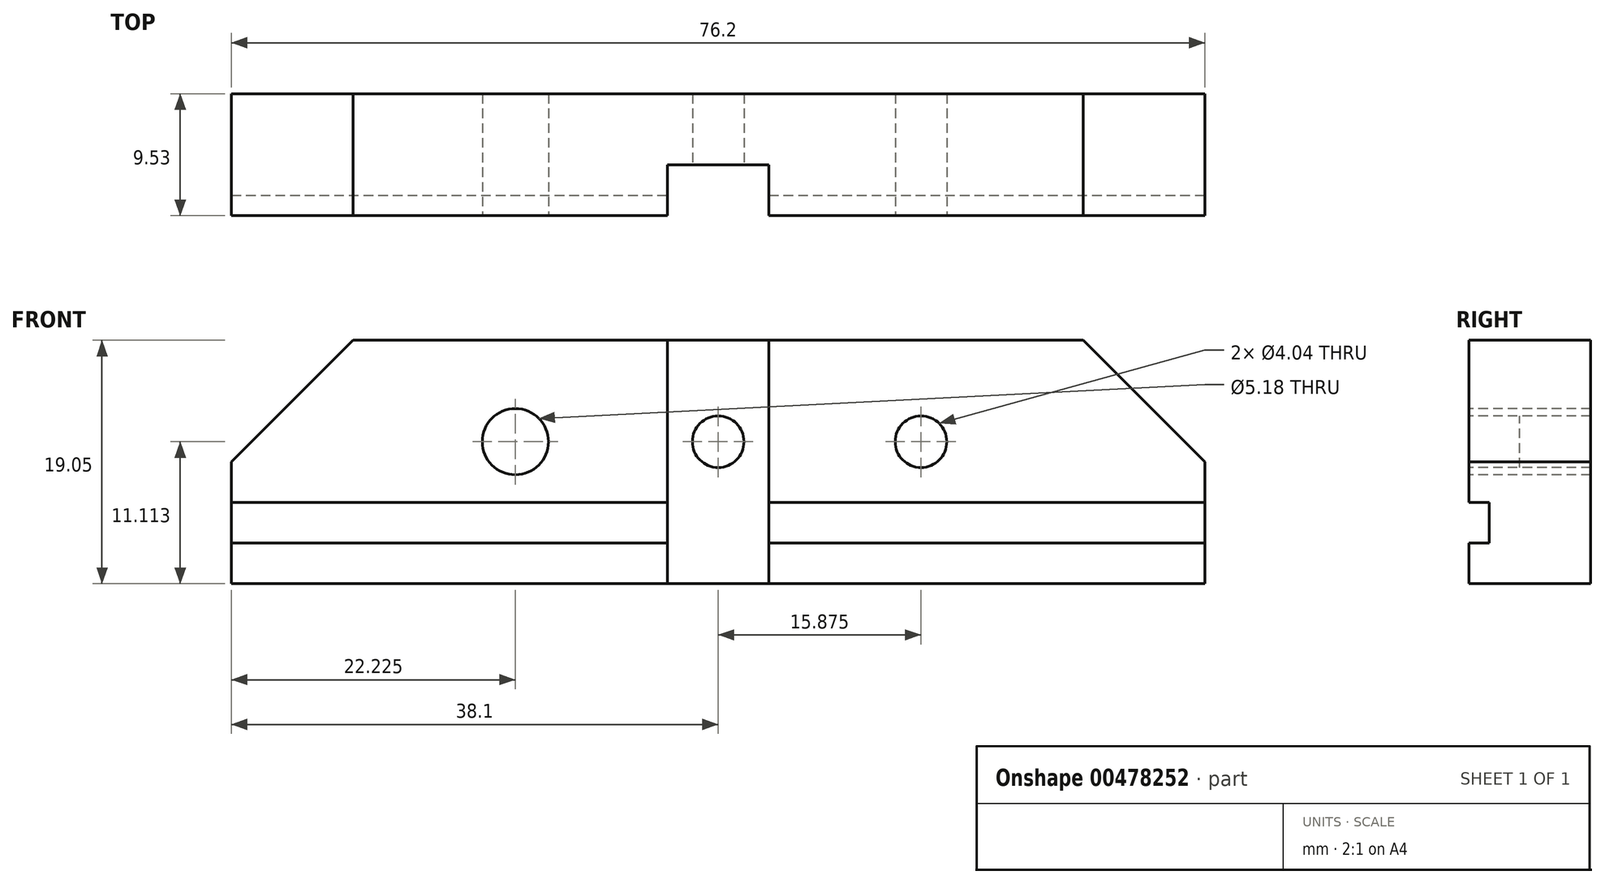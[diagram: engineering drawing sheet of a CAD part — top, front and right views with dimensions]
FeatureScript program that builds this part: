
annotation { "Feature Type Name" : "Feature", "Feature Type Description" : "" }
export const myFeature = defineFeature(function(context is Context, id is Id, definition is map)
    precondition{}
    {
        {
            var Q0;
            Q0=qCreatedBy(makeId("Front.planeOp"),FACE);
            var sketch = newSketch(context, id + "F0", { "sketchPlane" : qUnion([Q0])});
            skLineSegment(sketch, "E0.bottom", {"start": v(-38.1, 19.05) * mm, "end": v(38.1, 19.05) * mm});
            skLineSegment(sketch, "E0.top", {"start": v(-38.1, 0) * mm, "end": v(38.1, 0) * mm});
            skLineSegment(sketch, "E0.left", {"start": v(-38.1, 19.05) * mm, "end": v(-38.1, 0) * mm});
            skLineSegment(sketch, "E0.right", {"start": v(38.1, 19.05) * mm, "end": v(38.1, 0) * mm});
            skLineSegment(sketch, "E1", {"start": v(38.1, 11.11) * mm, "end": v(-38.1, 11.11) * mm, "construction": true});
            skLineSegment(sketch, "E2", {"start": v(-38.1, 6.35) * mm, "end": v(38.1, 6.35) * mm});
            skLineSegment(sketch, "E3", {"start": v(-38.1, 3.17) * mm, "end": v(38.1, 3.18) * mm});
            skLineSegment(sketch, "E4", {"start": v(-38.1, 4.76) * mm, "end": v(38.1, 4.76) * mm, "construction": true});
            skLineSegment(sketch, "E5", {"start": v(-3.97, 19.05) * mm, "end": v(-3.97, 0) * mm});
            skLineSegment(sketch, "E6", {"start": v(3.97, 0) * mm, "end": v(3.97, 19.05) * mm});
            skLineSegment(sketch, "E7", {"start": v(0, 19.05) * mm, "end": v(0, 0) * mm, "construction": true});
            skCircle(sketch, "E8", {"center": v(-15.88, 11.11) * mm, "radius": 2.6 * mm});
            skCircle(sketch, "E9", {"center": v(15.88, 11.11) * mm, "radius": 2.02 * mm});
            skCircle(sketch, "E10", {"center": v(0, 11.11) * mm, "radius": 2.02 * mm});
            skSolve(sketch);
        }
        {
            var Q0;
            Q0 = qSketchRegion(id + "F0", true);
            var Q1;
            {var subQ0=sQuery(id+"F0.wireOp",EDGE,"E5");var subQ1=sQuery(id+"F0.wireOp",EDGE,"E2");var subQ2=makeQuery(id+"F0.imprint","INTERSECT",VERTEX,{"derivedFrom":[subQ1,subQ0]});Q1=makeQuery(id+"F0.imprint","IMPRINT",FACE,{"disambiguationData":[TD([[makeQuery(id+"F0.imprint","IMPRINT",EDGE,{"disambiguationData":[TD([[subQ2,-1.0]])],"derivedFrom":subQ1}),-1.0]])]});}
            var Q2;
            Q2=makeQuery(id+"F0.imprint","IMPRINT",FACE,{"disambiguationData":[TD([[makeQuery(id+"F0.imprint","IMPRINT",EDGE,{"derivedFrom":sQuery(id+"F0.wireOp",EDGE,"E10")}),1.0]])]});
            var Q3;
            Q3=makeQuery(id+"F0.imprint","IMPRINT",FACE,{"disambiguationData":[TD([[makeQuery(id+"F0.imprint","IMPRINT",EDGE,{"derivedFrom":sQuery(id+"F0.wireOp",EDGE,"E9")}),1.0]])]});
            extrude(context, id + "F1", {"entities" : qUnion([Q0, Q1, Q2, Q3]), "oppositeDirection" : true, "depth" : 9.52 * mm, "offsetDistance" : 25.4 * mm});
        }
        {
            var Q0;
            Q0=makeQuery(id+"F0.imprint","IMPRINT",FACE,{"disambiguationData":[TD([[makeQuery(id+"F0.imprint","IMPRINT",EDGE,{"derivedFrom":sQuery(id+"F0.wireOp",EDGE,"E10")}),-1.0]])]});
            var Q1;
            {var subQ0=sQuery(id+"F0.wireOp",EDGE,"E5");var subQ1=sQuery(id+"F0.wireOp",EDGE,"E2");var subQ2=makeQuery(id+"F0.imprint","INTERSECT",VERTEX,{"derivedFrom":[subQ1,subQ0]});Q1=makeQuery(id+"F0.imprint","IMPRINT",FACE,{"disambiguationData":[TD([[makeQuery(id+"F0.imprint","IMPRINT",EDGE,{"disambiguationData":[TD([[subQ2,-1.0]])],"derivedFrom":subQ1}),-1.0]])]});}
            var Q2;
            {var subQ0=sQuery(id+"F0.wireOp",EDGE,"E5");var subQ1=sQuery(id+"F0.wireOp",EDGE,"E0.top");var subQ2=makeQuery(id+"F0.imprint","INTERSECT",VERTEX,{"derivedFrom":[subQ1,subQ0]});Q2=makeQuery(id+"F0.imprint","IMPRINT",FACE,{"disambiguationData":[TD([[makeQuery(id+"F0.imprint","IMPRINT",EDGE,{"disambiguationData":[TD([[subQ2,-1.0]])],"derivedFrom":subQ1}),1.0]])]});}
            extrude(context, id + "F2", {"entities" : qUnion([Q0, Q1, Q2]), "operationType" : NewBodyOperationType.REMOVE, "oppositeDirection" : true, "depth" : 3.96 * mm, "offsetDistance" : 25.4 * mm});
        }
        {
            var Q0;
            {var subQ0=sQuery(id+"F0.wireOp",EDGE,"E2");var subQ1=sQuery(id+"F0.wireOp",EDGE,"E0.left");var subQ2=makeQuery(id+"F0.imprint","INTERSECT",VERTEX,{"derivedFrom":[subQ1,subQ0]});Q0=makeQuery(id+"F0.imprint","IMPRINT",FACE,{"disambiguationData":[TD([[makeQuery(id+"F0.imprint","IMPRINT",EDGE,{"disambiguationData":[TD([[subQ2,-1.0]])],"derivedFrom":subQ1}),1.0]])]});}
            var Q1;
            {var subQ0=sQuery(id+"F0.wireOp",EDGE,"E2");var subQ1=sQuery(id+"F0.wireOp",EDGE,"E0.right");var subQ2=makeQuery(id+"F0.imprint","INTERSECT",VERTEX,{"derivedFrom":[subQ1,subQ0]});Q1=makeQuery(id+"F0.imprint","IMPRINT",FACE,{"disambiguationData":[TD([[makeQuery(id+"F0.imprint","IMPRINT",EDGE,{"disambiguationData":[TD([[subQ2,-1.0]])],"derivedFrom":subQ1}),-1.0]])]});}
            extrude(context, id + "F3", {"entities" : qUnion([Q0, Q1]), "operationType" : NewBodyOperationType.REMOVE, "oppositeDirection" : true, "depth" : 1.59 * mm, "offsetDistance" : 25.4 * mm});
        }
        {
            var Q0;
            Q0=makeQuery(id+"F1.opExtrude","SWEPT_EDGE",EDGE,{"disambiguationData":[OSD([sQuery(id+"F0.wireOp",EDGE,"E0.bottom"),sQuery(id+"F0.wireOp",EDGE,"E0.right")])]});
            var Q1;
            Q1=makeQuery(id+"F1.opExtrude","SWEPT_EDGE",EDGE,{"disambiguationData":[OSD([sQuery(id+"F0.wireOp",EDGE,"E0.bottom"),sQuery(id+"F0.wireOp",EDGE,"E0.left")])]});
            chamfer(context, id + "F4", {"entities" : qUnion([Q0, Q1]), "width" : 9.52 * mm, "tangentPropagation" : true});
        }
        {
            var Q0;
            Q0=sQuery(id+"F0.wireOp",VERTEX,"E10.center");
            var Q1;
            Q1=sQuery(id+"F0.wireOp",VERTEX,"E9.center");
            var Q2;
            Q2=makeQuery(id+"F1.opExtrude","SWEPT_BODY",BODY,{"disambiguationData":[OSD([sQuery(id+"F0.wireOp",EDGE,"E0.bottom"),sQuery(id+"F0.wireOp",EDGE,"E0.top"),sQuery(id+"F0.wireOp",EDGE,"E0.left"),sQuery(id+"F0.wireOp",EDGE,"E0.right"),sQuery(id+"F0.wireOp",EDGE,"E8")])]});
            hole(context, id + "F5", {"style" : HoleStyle.SIMPLE, "endStyle" : HoleEndStyle.THROUGH, "standardTappedOrClearance" : lookupTablePath({ "standard" : "ANSI", "engagement" : "75%", "pitch" : "32 tpi", "size" : "#10", "type" : "Tapped" }), "standardBlindInLast" : lookupTablePath({ "standard" : "ANSI", "fit" : "Normal", "engagement" : "75%", "pitch" : "32 tpi", "size" : "#10", "type" : "Clearance & tapped" }), "holeDiameter" : 4.04 * mm, "majorDiameter" : 4.83 * mm, "showTappedDepth" : true, "isTappedThrough" : true, "tappedDepth" : 7.43 * mm, "tapClearance" : 3, "locations" : qUnion([Q0, Q1]), "scope" : qUnion([Q2])});
        }
    });
